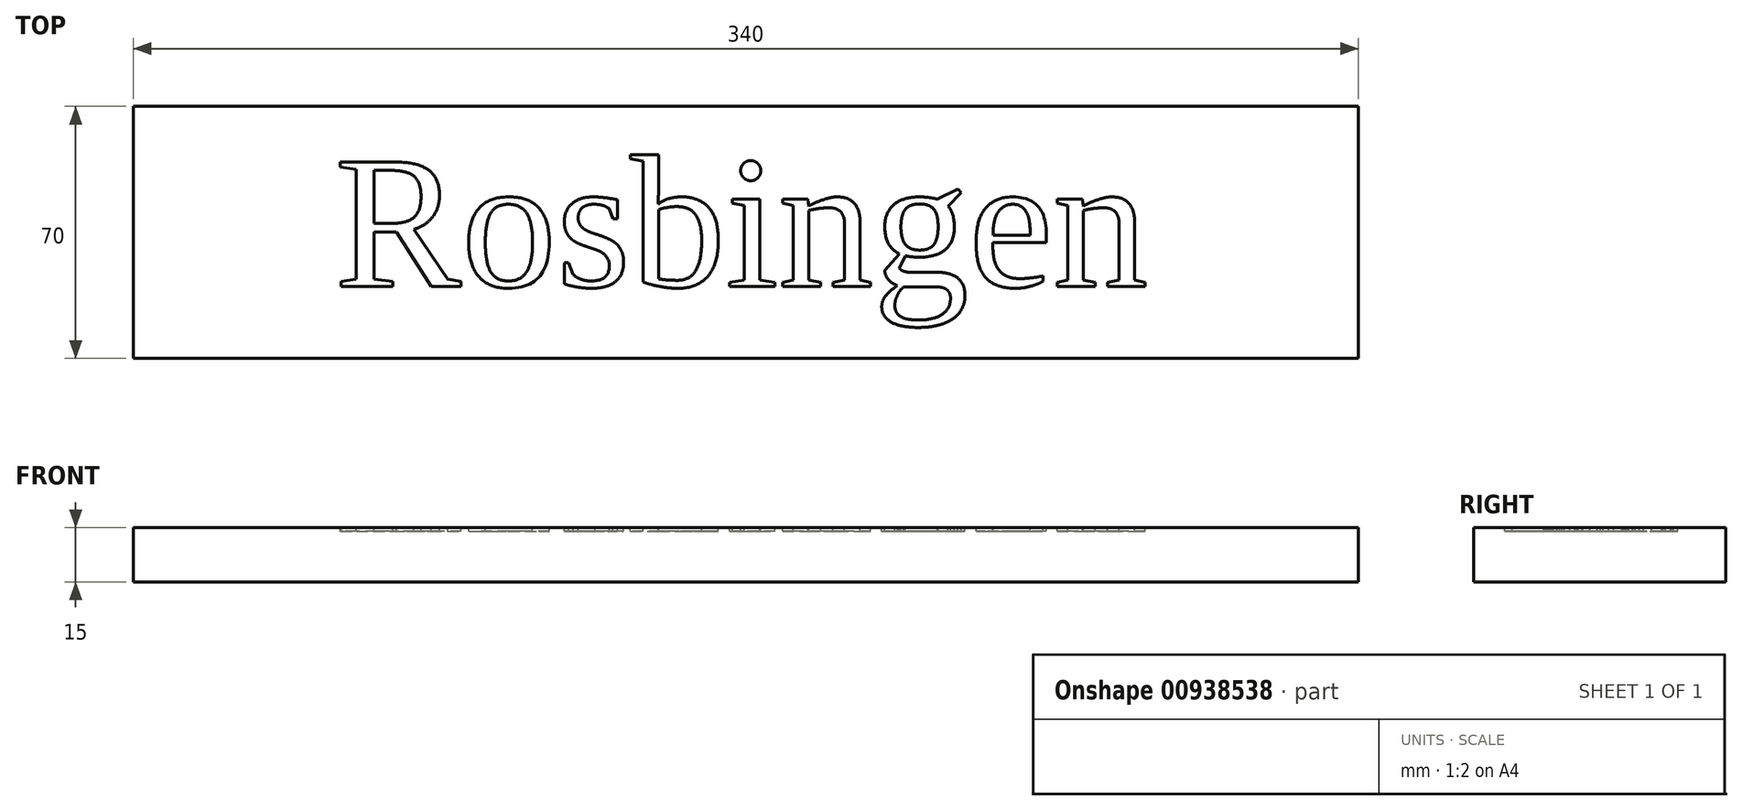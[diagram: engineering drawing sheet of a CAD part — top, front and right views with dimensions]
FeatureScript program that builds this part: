
annotation { "Feature Type Name" : "Feature", "Feature Type Description" : "" }
export const myFeature = defineFeature(function(context is Context, id is Id, definition is map)
    precondition{}
    {
        {
            var Q0;
            Q0=qCreatedBy(makeId("Top.planeOp"),FACE);
            var sketch = newSketch(context, id + "F0", { "sketchPlane" : qUnion([Q0])});
            skLineSegment(sketch, "E0.bottom", {"start": v(-168.85, 80.75) * mm, "end": v(171.15, 80.75) * mm});
            skLineSegment(sketch, "E0.top", {"start": v(-168.85, 10.75) * mm, "end": v(171.15, 10.75) * mm});
            skLineSegment(sketch, "E0.left", {"start": v(-168.85, 80.75) * mm, "end": v(-168.85, 10.75) * mm});
            skLineSegment(sketch, "E0.right", {"start": v(171.15, 80.75) * mm, "end": v(171.15, 10.75) * mm});
            skLineSegment(sketch, "E1", {"start": v(1.15, 10.75) * mm, "end": v(1.15, 80.75) * mm, "construction": true});
            skSolve(sketch);
        }
        {
            var Q0;
            Q0=qSketchRegion(id+"F0",true);
            extrude(context, id + "F1", {"entities" : qUnion([Q0]), "depth" : 15 * mm, "offsetDistance" : 25 * mm});
        }
        {
            var Q0;
            Q0=makeQuery(id+"F1.opExtrude","CAP_FACE",FACE,{"disambiguationData":[OSD([sQuery(id+"F0.wireOp",EDGE,"E0.bottom"),sQuery(id+"F0.wireOp",EDGE,"E0.top"),sQuery(id+"F0.wireOp",EDGE,"E0.left"),sQuery(id+"F0.wireOp",EDGE,"E0.right")])],"isStart":false});
            var sketch = newSketch(context, id + "F2", { "sketchPlane" : qUnion([Q0])});
            skText(sketch, "E2", { "text": "Rosbingen", "fontName": "Tinos-Regular.ttf"});
            skLineSegment(sketch, "E3", {"start": v(1.15, 80.75) * mm, "end": v(1.15, 10.75) * mm, "construction": true});
            const initialGuessF2  = {"E2": [-0.113, 0.03075, 1, 0, 0.038]};
            skSetInitialGuess(sketch, initialGuessF2);
            skSolve(sketch);
        }
        {
            var Q0;
            Q0=qSketchRegion(id+"F2",true);
            extrude(context, id + "F3", {"entities" : qUnion([Q0]), "operationType" : NewBodyOperationType.REMOVE, "oppositeDirection" : true, "depth" : 1 * mm, "offsetDistance" : 25 * mm});
        }
    });
